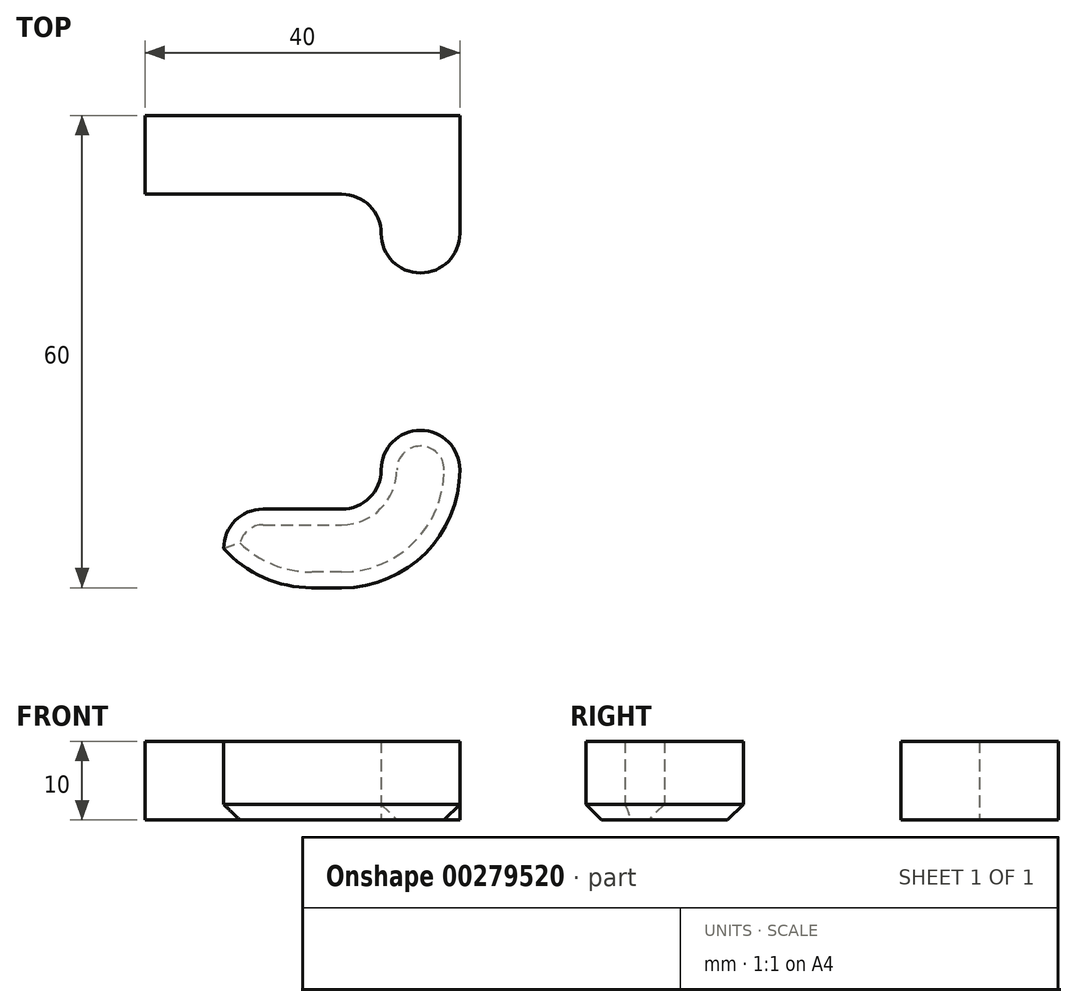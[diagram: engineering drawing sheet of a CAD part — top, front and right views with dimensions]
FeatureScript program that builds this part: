
annotation { "Feature Type Name" : "Feature", "Feature Type Description" : "" }
export const myFeature = defineFeature(function(context is Context, id is Id, definition is map)
    precondition{}
    {
        {
            var Q0;
            Q0=qCreatedBy(makeId("Top.planeOp"),FACE);
            var sketch = newSketch(context, id + "F0", { "sketchPlane" : qUnion([Q0])});
            skLineSegment(sketch, "E0.bottom", {"start": v(-10.46, 17.68) * mm, "end": v(-0.46, 17.68) * mm});
            skLineSegment(sketch, "E0.top", {"start": v(-10.46, 37.68) * mm, "end": v(-0.46, 37.68) * mm});
            skLineSegment(sketch, "E0.left", {"start": v(-10.46, 17.68) * mm, "end": v(-10.46, 37.68) * mm});
            skLineSegment(sketch, "E0.right", {"start": v(-0.46, 17.68) * mm, "end": v(-0.46, 37.68) * mm});
            skLineSegment(sketch, "E1.bottom", {"start": v(-10.46, 37.68) * mm, "end": v(-40.46, 37.68) * mm});
            skLineSegment(sketch, "E1.top", {"start": v(-10.46, 27.68) * mm, "end": v(-40.46, 27.68) * mm});
            skLineSegment(sketch, "E1.left", {"start": v(-10.46, 37.68) * mm, "end": v(-10.46, 27.68) * mm});
            skLineSegment(sketch, "E1.right", {"start": v(-40.46, 37.68) * mm, "end": v(-40.46, 27.68) * mm});
            skLineSegment(sketch, "E2.bottom", {"start": v(-40.46, 27.68) * mm, "end": v(-30.46, 27.68) * mm});
            skLineSegment(sketch, "E2.top", {"start": v(-40.46, -22.32) * mm, "end": v(-30.46, -22.32) * mm});
            skLineSegment(sketch, "E2.left", {"start": v(-40.46, 27.68) * mm, "end": v(-40.46, -22.32) * mm});
            skLineSegment(sketch, "E2.right", {"start": v(-30.46, 27.68) * mm, "end": v(-30.46, -22.32) * mm});
            skLineSegment(sketch, "E3.bottom", {"start": v(-30.46, -22.32) * mm, "end": v(-0.46, -22.32) * mm});
            skLineSegment(sketch, "E3.top", {"start": v(-30.46, -12.32) * mm, "end": v(-0.46, -12.32) * mm});
            skLineSegment(sketch, "E3.left", {"start": v(-30.46, -22.32) * mm, "end": v(-30.46, -12.32) * mm});
            skLineSegment(sketch, "E3.right", {"start": v(-0.46, -22.32) * mm, "end": v(-0.46, -12.32) * mm});
            skLineSegment(sketch, "E4.bottom", {"start": v(-10.46, -2.32) * mm, "end": v(-0.46, -2.32) * mm});
            skLineSegment(sketch, "E4.top", {"start": v(-10.46, -12.32) * mm, "end": v(-0.46, -12.32) * mm});
            skLineSegment(sketch, "E4.left", {"start": v(-10.46, -2.32) * mm, "end": v(-10.46, -12.32) * mm});
            skLineSegment(sketch, "E4.right", {"start": v(-0.46, -2.32) * mm, "end": v(-0.46, -12.32) * mm});
            skSolve(sketch);
        }
        {
            var Q0;
            Q0=makeQuery(id+"F0.imprint","IMPRINT",FACE,{"disambiguationData":[TD([[makeQuery(id+"F0.imprint","IMPRINT",EDGE,{"derivedFrom":sQuery(id+"F0.wireOp",EDGE,"E0.bottom")}),1.0]])]});
            var Q1;
            Q1=makeQuery(id+"F0.imprint","IMPRINT",FACE,{"disambiguationData":[TD([[makeQuery(id+"F0.imprint","IMPRINT",EDGE,{"derivedFrom":sQuery(id+"F0.wireOp",EDGE,"E1.bottom")}),1.0]])]});
            var Q2;
            Q2=makeQuery(id+"F0.imprint","IMPRINT",FACE,{"disambiguationData":[TD([[makeQuery(id+"F0.imprint","IMPRINT",EDGE,{"derivedFrom":sQuery(id+"F0.wireOp",EDGE,"E2.bottom")}),-1.0]])]});
            var Q3;
            Q3=makeQuery(id+"F0.imprint","IMPRINT",FACE,{"disambiguationData":[TD([[makeQuery(id+"F0.imprint","IMPRINT",EDGE,{"derivedFrom":sQuery(id+"F0.wireOp",EDGE,"E3.bottom")}),1.0]])]});
            var Q4;
            Q4=makeQuery(id+"F0.imprint","IMPRINT",FACE,{"disambiguationData":[TD([[makeQuery(id+"F0.imprint","IMPRINT",EDGE,{"derivedFrom":sQuery(id+"F0.wireOp",EDGE,"E4.bottom")}),-1.0]])]});
            extrude(context, id + "F1", {"entities" : qUnion([Q0, Q1, Q2, Q3, Q4]), "depth" : 10 * mm});
        }
        {
            var Q0;
            Q0=makeQuery(id+"F1.opExtrude","SWEPT_EDGE",EDGE,{"disambiguationData":[OSD([sQuery(id+"F0.wireOp",EDGE,"E0.bottom"),sQuery(id+"F0.wireOp",EDGE,"E0.right")])]});
            var Q1;
            Q1=makeQuery(id+"F1.opExtrude","SWEPT_EDGE",EDGE,{"disambiguationData":[OSD([sQuery(id+"F0.wireOp",EDGE,"E0.bottom"),sQuery(id+"F0.wireOp",EDGE,"E0.left")])]});
            var Q2;
            Q2=makeQuery(id+"F1.opExtrude","SWEPT_EDGE",EDGE,{"disambiguationData":[OSD([sQuery(id+"F0.wireOp",EDGE,"E0.left"),sQuery(id+"F0.wireOp",EDGE,"E1.top"),sQuery(id+"F0.wireOp",EDGE,"E1.left")])]});
            var Q3;
            Q3=makeQuery(id+"F1.opExtrude","SWEPT_EDGE",EDGE,{"disambiguationData":[OSD([sQuery(id+"F0.wireOp",EDGE,"E1.top"),sQuery(id+"F0.wireOp",EDGE,"E2.bottom"),sQuery(id+"F0.wireOp",EDGE,"E2.right")])]});
            var Q4;
            Q4=makeQuery(id+"F1.opExtrude","SWEPT_EDGE",EDGE,{"disambiguationData":[OSD([sQuery(id+"F0.wireOp",EDGE,"E2.right"),sQuery(id+"F0.wireOp",EDGE,"E3.top"),sQuery(id+"F0.wireOp",EDGE,"E3.left")])]});
            var Q5;
            Q5=makeQuery(id+"F1.opExtrude","SWEPT_EDGE",EDGE,{"disambiguationData":[OSD([sQuery(id+"F0.wireOp",EDGE,"E3.top"),sQuery(id+"F0.wireOp",EDGE,"E4.top"),sQuery(id+"F0.wireOp",EDGE,"E4.left")])]});
            var Q6;
            Q6=makeQuery(id+"F1.opExtrude","SWEPT_EDGE",EDGE,{"disambiguationData":[OSD([sQuery(id+"F0.wireOp",EDGE,"E4.bottom"),sQuery(id+"F0.wireOp",EDGE,"E4.left")])]});
            var Q7;
            Q7=makeQuery(id+"F1.opExtrude","SWEPT_EDGE",EDGE,{"disambiguationData":[OSD([sQuery(id+"F0.wireOp",EDGE,"E4.bottom"),sQuery(id+"F0.wireOp",EDGE,"E4.right")])]});
            fillet(context, id + "F2", {"entities" : qUnion([Q0, Q1, Q2, Q3, Q4, Q5, Q6, Q7]), "radius" : 5 * mm, "tangentPropagation" : true, "allowEdgeOverflow" : false});
        }
        {
            var Q0;
            Q0=makeQuery(id+"F1.opExtrude","SWEPT_EDGE",EDGE,{"disambiguationData":[OSD([sQuery(id+"F0.wireOp",EDGE,"E0.top"),sQuery(id+"F0.wireOp",EDGE,"E0.right")])]});
            var Q1;
            Q1=makeQuery(id+"F1.opExtrude","SWEPT_EDGE",EDGE,{"disambiguationData":[OSD([sQuery(id+"F0.wireOp",EDGE,"E1.bottom"),sQuery(id+"F0.wireOp",EDGE,"E1.right")])]});
            var Q2;
            Q2=makeQuery(id+"F1.opExtrude","SWEPT_EDGE",EDGE,{"disambiguationData":[OSD([sQuery(id+"F0.wireOp",EDGE,"E3.bottom"),sQuery(id+"F0.wireOp",EDGE,"E3.right")])]});
            var Q3;
            Q3=makeQuery(id+"F1.opExtrude","SWEPT_EDGE",EDGE,{"disambiguationData":[OSD([sQuery(id+"F0.wireOp",EDGE,"E2.top"),sQuery(id+"F0.wireOp",EDGE,"E2.left")])]});
            fillet(context, id + "F3", {"entities" : qUnion([Q0, Q1, Q2, Q3]), "radius" : 15 * mm, "tangentPropagation" : true, "allowEdgeOverflow" : false});
        }
        {
            var Q0;
            Q0=makeQuery(id+"F1.opExtrude","CAP_EDGE",EDGE,{"disambiguationData":[OSD([sQuery(id+"F0.wireOp",EDGE,"E2.right")])],"isStart":false});
            var Q1;
            {var subQ0=sQuery(id+"F0.wireOp",EDGE,"E3.right");var subQ1=sQuery(id+"F0.wireOp",EDGE,"E3.bottom");Q1=makeQuery(id+"F3.opFillet","BLEND_EDGE",EDGE,{"blendedFrom":[makeQuery(id+"F1.opExtrude","SWEPT_EDGE",EDGE,{"disambiguationData":[OSD([subQ1,subQ0])]}),makeQuery(id+"F1.opExtrude","CAP_FACE",FACE,{"disambiguationData":[OSD([sQuery(id+"F0.wireOp",EDGE,"E0.bottom"),sQuery(id+"F0.wireOp",EDGE,"E0.top"),sQuery(id+"F0.wireOp",EDGE,"E0.left"),sQuery(id+"F0.wireOp",EDGE,"E0.right"),sQuery(id+"F0.wireOp",EDGE,"E1.bottom"),sQuery(id+"F0.wireOp",EDGE,"E1.top"),sQuery(id+"F0.wireOp",EDGE,"E1.right"),sQuery(id+"F0.wireOp",EDGE,"E2.top"),sQuery(id+"F0.wireOp",EDGE,"E2.left"),sQuery(id+"F0.wireOp",EDGE,"E2.right"),subQ1,sQuery(id+"F0.wireOp",EDGE,"E3.top"),subQ0,sQuery(id+"F0.wireOp",EDGE,"E4.bottom"),sQuery(id+"F0.wireOp",EDGE,"E4.left"),sQuery(id+"F0.wireOp",EDGE,"E4.right")])],"isStart":true})],"blendedInto":[makeQuery(id+"F1.opExtrude","CAP_FACE",FACE,{"disambiguationData":[OSD([sQuery(id+"F0.wireOp",EDGE,"E0.bottom"),sQuery(id+"F0.wireOp",EDGE,"E0.top"),sQuery(id+"F0.wireOp",EDGE,"E0.left"),sQuery(id+"F0.wireOp",EDGE,"E0.right"),sQuery(id+"F0.wireOp",EDGE,"E1.bottom"),sQuery(id+"F0.wireOp",EDGE,"E1.top"),sQuery(id+"F0.wireOp",EDGE,"E1.right"),sQuery(id+"F0.wireOp",EDGE,"E2.top"),sQuery(id+"F0.wireOp",EDGE,"E2.left"),sQuery(id+"F0.wireOp",EDGE,"E2.right"),subQ1,sQuery(id+"F0.wireOp",EDGE,"E3.top"),subQ0,sQuery(id+"F0.wireOp",EDGE,"E4.bottom"),sQuery(id+"F0.wireOp",EDGE,"E4.left"),sQuery(id+"F0.wireOp",EDGE,"E4.right")])],"isStart":true})]});}
            chamfer(context, id + "F4", {"entities" : qUnion([Q0, Q1]), "width" : 2 * mm, "tangentPropagation" : true});
        }
    });
